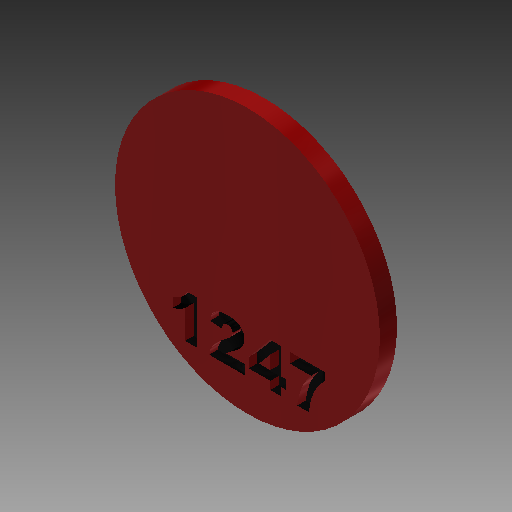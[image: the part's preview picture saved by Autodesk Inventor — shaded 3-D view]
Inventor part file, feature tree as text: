
AUTODESK INVENTOR PART (.ipt)
format: ipt  version: 2017.2 (Build 212233000, 233)  size: 655,872 bytes
history: native  units: in
note: dims shown in document units (in); Inventor stores cm internally (conversion verified against a paired STEP export)
features: sketch x23, extrude x17, plane x9, projected_geometry x5, loft x4, other x3, mirror x1, emboss x1, fillet x1
ambient origin geometry x8: Origin, YZ Plane, XZ Plane, XY Plane, X Axis, Y Axis, Z Axis, Center Point
bodies: Solid1 (feature_tree)
feature tree (64):
  sketch  "Sketch1"  dims[d0=0.7559in d1=0.7559in]
  plane  "Work Plane1"
  loft  "Loft1"
  extrude  "Extrusion1"  Depth=0.2in
  plane  "Work Plane4"
  loft  "Loft2"
  plane  "Work Plane5"
  loft  "Loft3"
  loft  "Loft4"
  extrude  "Extrusion2"  TaperAngle=0.0deg  [1 undecoded]
  plane  "Work Plane6"
  extrude  "Extrusion3"  Depth=1.0in
  extrude  "Extrusion4"  Depth=1.0651in
  extrude  "Extrusion5"  Depth=0.962in
  plane  "Work Plane7"
  extrude  "Extrusion6"  Depth=0.075in
  plane  "Work Plane8"
  other  "Work Axis1"
  plane  "Work Plane9"
  extrude  "Extrusion7"  Depth=0.06in
  mirror  "Mirror3"
  extrude  "Extrusion8"  Depth=0.05in
  plane  "Work Plane10"
  extrude  "Extrusion9"  Depth=0.0625in
  plane  "Work Plane11"
  extrude  "Extrusion10"  Depth=0.075in
  extrude  "Extrusion11"  TaperAngle=0.0deg  [1 undecoded]
  extrude  "Extrusion12"  Depth=0.2in
  extrude  "Extrusion13"  TaperAngle=0.0deg  [1 undecoded]
  emboss  "Emboss1"
  extrude  "Extrusion16"  Depth=0.01in
  extrude  "Extrusion17"  Depth=0.0344in
  extrude  "Extrusion18"  TaperAngle=60.0deg  [1 undecoded]
  fillet  "Fillet1"  [1 undecoded]
  extrude  "Extrusion20"  Depth=0.05in
  sketch  "Sketch2"  dims[d2=0.9963in d3=0.2in]
  sketch  "Sketch3"  dims[d4=0.5in d6=0.08in]
  sketch  "Sketch4"  dims[d7=0.55in d8=150.0deg]
  other  "Edges1"
  sketch  "Sketch5"  dims[d9=150.0deg d14=0.33in]
  projected_geometry  "Projected Loop1"
  other  "Edges2"
  sketch  "Sketch6"  dims[d15=0.66in d18=0.0in d19=90.0deg]
  sketch  "Sketch7"  dims[d20=0.0in d21=90.0deg d22=1.0in]
  sketch  "Sketch8"  dims[d26=1.0651in d28=1.0651in]
  sketch  "Sketch9"  dims[d29=0.0in d30=0.962in]
  sketch  "Sketch10"  dims[d31=0.962in d32=0.075in]
  sketch  "Sketch11"  dims[d33=0.15in d34=0.06in]
  sketch  "Sketch12"  dims[d35=0.1in d36=0.05in]
  sketch  "Sketch13"  dims[d37=0.45in d38=0.0in d39=0.0625in]
  projected_geometry  "Projected Loop2"
  projected_geometry  "Projected Loop3"
  sketch  "Sketch14"  dims[d40=0.01in d41=0.075in]
  projected_geometry  "Projected Loop4"
  sketch  "Sketch15"  dims[d42=0.01in d43=0.0in d44=90.0deg]
  sketch  "Sketch16"  dims[d45=0.0in d46=90.0deg d47=0.2in]
  sketch  "Sketch17"  dims[d48=0.07in d49=0.0in d50=90.0deg]
  sketch  "Sketch18"  dims[d51=0.0in d52=90.0deg d53=0.01in]
  sketch  "Sketch19"  dims[d54=0.01in d55=0.0344in]
  sketch  "Sketch23"  dims[d56=150.0deg d57=60.0deg d58=150.0deg]
  projected_geometry  "Projected Loop6"
  sketch  "Sketch24"  dims[d59=0.7in d60=0.05in]
  sketch  "Sketch25"  dims[d61=0.05in d62=0.05in]
  sketch  "Sketch27"  dims[d63=0.05in d64=0.05in d65=0.01in d66=0.0in d67=90.0deg d68=0.0in d69=90.0deg d70=0.1in d71=0.4in d72=0.15in d73=0.05in d74=0.0in d75=0.02in d77=0.15in d78=0.02in d79=0.1in d80=0.1in d81=0.1in d82=0.02in d83=0.15in d84=0.05in d85=0.0in d86=0.045in d87=0.0in d88=0.025in d89=0.0in d90=0.02in d91=0.02in d92=0.005in d93=0.0in d94=90.0deg d95=0.4466in d96=1.0in d97=0.0in d98=1.0in d99=0.0in d100=0.6528in d101=0.0in d102=0.0in d103=1.0in d104=0.0in d106=90.0deg d107=1.0in d108=0.0in d109=1.65in d110=0.1in d111=0.1in d112=0.0in d113=0.1in d114=0.075in d115=0.0in d116=0.05in d117=0.0in d123=0.84in d124=0.8in d125=0.0in d126=0.0in d127=1.0in d128=0.0in d130=0.15in d131=-0.0206in d135=0.2in d136=0.05in d137=0.1in d140=0.05in d141=0.1in d142=0.0in]
note: 5 required parameter values undecoded (feature->parameter linkage not recoverable at this tier; creation-order binding heuristic only, values carry confidence <= 0.55)
